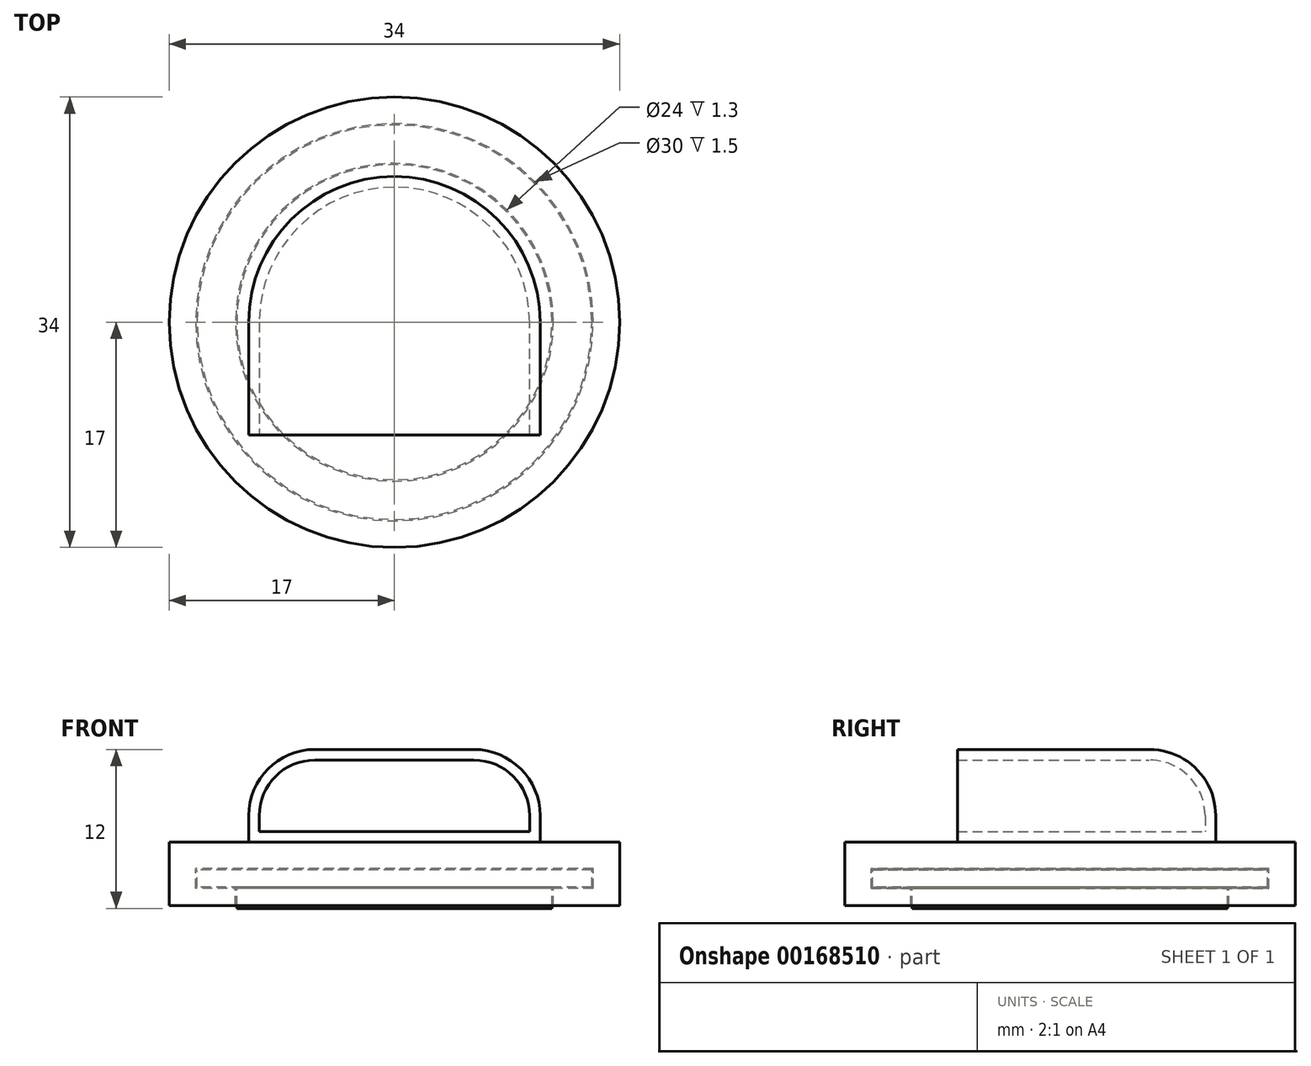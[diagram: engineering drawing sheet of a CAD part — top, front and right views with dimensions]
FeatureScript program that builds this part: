
annotation { "Feature Type Name" : "Feature", "Feature Type Description" : "" }
export const myFeature = defineFeature(function(context is Context, id is Id, definition is map)
    precondition{}
    {
        {
            var Q0;
            Q0=qCreatedBy(makeId("Front.planeOp"),FACE);
            var sketch = newSketch(context, id + "F0", { "sketchPlane" : qUnion([Q0])});
            skLineSegment(sketch, "E0.bottom", {"start": v(15, 1.5) * mm, "end": v(-15, 1.5) * mm});
            skLineSegment(sketch, "E0.top", {"start": v(15, -1.5) * mm, "end": v(-15, -1.5) * mm});
            skLineSegment(sketch, "E0.left", {"start": v(15, 1.5) * mm, "end": v(15, 0) * mm});
            skLineSegment(sketch, "E0.right", {"start": v(-15, 1.5) * mm, "end": v(-15, 0) * mm});
            skPoint(sketch, "E0.middle", {"position": v(0, 0) * mm});
            skLineSegment(sketch, "E1", {"start": v(-15, 0) * mm, "end": v(-12, 0) * mm});
            skPoint(sketch, "E1.endSnap0", {"position": v(-15, 0) * mm});
            skLineSegment(sketch, "E2", {"start": v(-12, 0) * mm, "end": v(-12, -1.5) * mm});
            skLineSegment(sketch, "E3.MirrorCS", {"start": v(15, 0) * mm, "end": v(12, 0) * mm});
            skLineSegment(sketch, "E4.MirrorCS", {"start": v(12, 0) * mm, "end": v(12, -1.5) * mm});
            skLineSegment(sketch, "E5", {"start": v(-17, -1.5) * mm, "end": v(-17, 3.5) * mm});
            skLineSegment(sketch, "E6", {"start": v(-17, 3.5) * mm, "end": v(17, 3.5) * mm});
            skLineSegment(sketch, "E7", {"start": v(17, 3.5) * mm, "end": v(17, -1.5) * mm});
            skLineSegment(sketch, "E8", {"start": v(17, -1.5) * mm, "end": v(15, -1.5) * mm});
            skLineSegment(sketch, "E9", {"start": v(-17, -1.5) * mm, "end": v(-15, -1.5) * mm});
            skLineSegment(sketch, "E10.0", {"start": v(-11.9, 0.1) * mm, "end": v(-11.9, -1.5) * mm});
            skLineSegment(sketch, "E10.1", {"start": v(-14.9, 0.1) * mm, "end": v(-11.9, 0.1) * mm});
            skLineSegment(sketch, "E10.2", {"start": v(-14.9, 1.4) * mm, "end": v(-14.9, 0.1) * mm});
            skLineSegment(sketch, "E10.3", {"start": v(11.9, 0.1) * mm, "end": v(11.9, -1.5) * mm});
            skLineSegment(sketch, "E10.4", {"start": v(14.9, 0.1) * mm, "end": v(11.9, 0.1) * mm});
            skLineSegment(sketch, "E10.5", {"start": v(14.9, 1.4) * mm, "end": v(14.9, 0.1) * mm});
            skLineSegment(sketch, "E10.6", {"start": v(14.9, 1.4) * mm, "end": v(-14.9, 1.4) * mm});
            skLineSegment(sketch, "E11", {"start": v(0, 8.78) * mm, "end": v(0, -4.34) * mm});
            skLineSegment(sketch, "E12", {"start": v(-17, -1.3) * mm, "end": v(-12, -1.3) * mm});
            skSolve(sketch);
        }
        {
            var Q0;
            {var subQ0=sQuery(id+"F0.wireOp",EDGE,"E0.right");Q0=makeQuery(id+"F0.imprint","IMPRINT",FACE,{"disambiguationData":[TD([[makeQuery(id+"F0.imprint","IMPRINT",EDGE,{"derivedFrom":subQ0}),-1.0]])]});}
            var Q1;
            Q1=sQuery(id+"F0.wireOp",EDGE,"E11");
            revolve(context, id + "F1", {"entities" : qUnion([Q0]), "axis" : qUnion([Q1]), "revolveType" : RevolveType.FULL});
        }
        {
            var Q0;
            {var subQ1=sQuery(id+"F0.wireOp",EDGE,"E10.0");Q0=makeQuery(id+"F0.imprint","IMPRINT",FACE,{"disambiguationData":[TD([[makeQuery(id+"F0.imprint","IMPRINT",EDGE,{"derivedFrom":subQ1}),1.0]])]});}
            var Q1;
            Q1=sQuery(id+"F0.wireOp",EDGE,"E11");
            revolve(context, id + "F2", {"entities" : qUnion([Q0]), "axis" : qUnion([Q1]), "revolveType" : RevolveType.FULL});
        }
        {
            var Q0;
            Q0=makeQuery(id+"F1.opRevolve","SWEPT_FACE",FACE,{"disambiguationData":[OSD([sQuery(id+"F0.wireOp",EDGE,"E6")])]});
            cPlane(context, id + "F3", {"entities" : qUnion([Q0]), "cplaneType" : CPlaneType.OFFSET, "offset" : 0 * mm, "width" : 150 * mm, "height" : 150 * mm});
        }
        {
            var Q0;
            Q0=qCreatedBy(id+"F3.planeOp",FACE);
            var sketch = newSketch(context, id + "F4", { "sketchPlane" : qUnion([Q0])});
            skCircle(sketch, "E13", {"center": v(0, 0) * mm, "radius": 17 * mm});
            skArc(sketch, "E14", {"start": v(11, 0) * mm, "mid": v(0, 11) * mm, "end": v(-11, 0) * mm});
            skLineSegment(sketch, "E15", {"start": v(-11, 0) * mm, "end": v(-11, -8.5) * mm});
            skLineSegment(sketch, "E16", {"start": v(-11, -8.5) * mm, "end": v(11, -8.5) * mm});
            skLineSegment(sketch, "E17", {"start": v(11, -8.5) * mm, "end": v(11, 0) * mm});
            skArc(sketch, "E18.0", {"start": v(7.3, 0) * mm, "mid": v(0, 7.3) * mm, "end": v(-7.3, 0) * mm});
            skLineSegment(sketch, "E18.1", {"start": v(7.3, -4.8) * mm, "end": v(7.3, 0) * mm});
            skLineSegment(sketch, "E18.3", {"start": v(-7.3, 0) * mm, "end": v(-7.3, -4.8) * mm});
            skLineSegment(sketch, "E19", {"start": v(-7.3, -4.8) * mm, "end": v(-7.3, -8.5) * mm});
            skLineSegment(sketch, "E20", {"start": v(7.3, -4.8) * mm, "end": v(7.3, -8.5) * mm});
            skSolve(sketch);
        }
        {
            var Q0;
            Q0=makeQuery(id+"F4.imprint","IMPRINT",FACE,{"disambiguationData":[TD([[makeQuery(id+"F4.imprint","IMPRINT",EDGE,{"derivedFrom":sQuery(id+"F4.wireOp",EDGE,"E14")}),1.0]])]});
            var Q1;
            Q1=makeQuery(id+"F4.imprint","IMPRINT",FACE,{"disambiguationData":[TD([[makeQuery(id+"F4.imprint","IMPRINT",EDGE,{"derivedFrom":sQuery(id+"F4.wireOp",EDGE,"E18.0")}),1.0]])]});
            extrude(context, id + "F5", {"entities" : qUnion([Q0, Q1]), "depth" : 7 * mm});
        }
        {
            var Q0;
            Q0=makeQuery(id+"F5.opExtrude","CAP_EDGE",EDGE,{"disambiguationData":[OSD([sQuery(id+"F4.wireOp",EDGE,"E15")])],"isStart":false});
            fillet(context, id + "F6", {"entities" : qUnion([Q0]), "radius" : 5 * mm, "tangentPropagation" : true, "allowEdgeOverflow" : false});
        }
        {
            var Q0;
            Q0=makeQuery(id+"F5.opExtrude","SWEPT_FACE",FACE,{"disambiguationData":[OSD([sQuery(id+"F4.wireOp",EDGE,"E16")])]});
            shell(context, id + "F7", {"entities" : qUnion([Q0]), "thickness" : .8 * mm});
        }
    });
